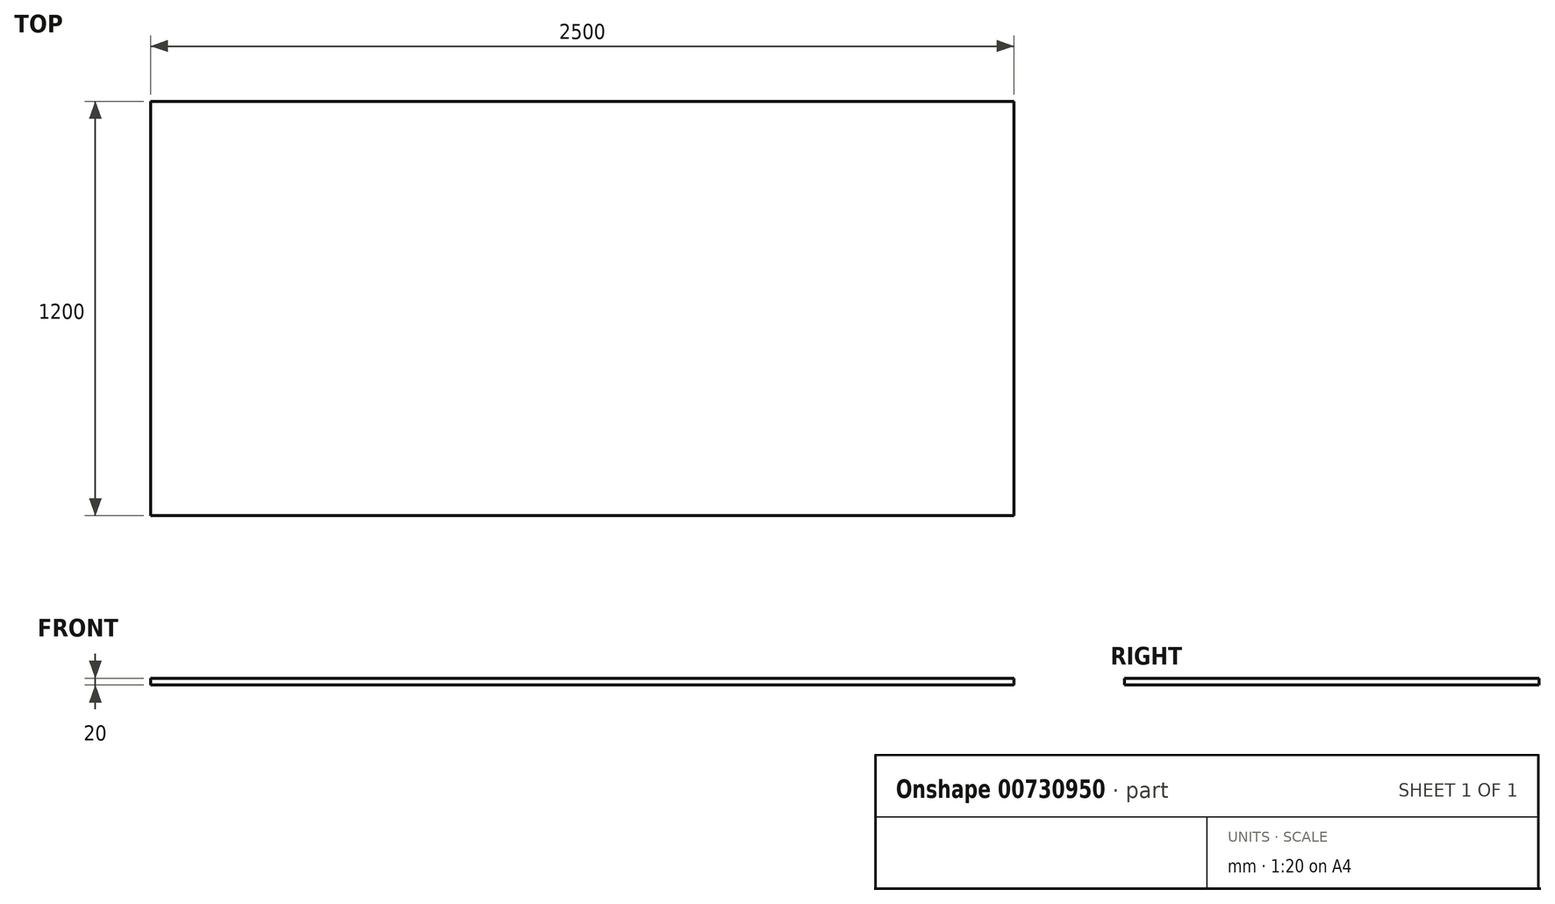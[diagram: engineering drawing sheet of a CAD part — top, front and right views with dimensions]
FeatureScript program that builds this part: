
annotation { "Feature Type Name" : "Feature", "Feature Type Description" : "" }
export const myFeature = defineFeature(function(context is Context, id is Id, definition is map)
    precondition{}
    {
        {
            var Q0;
            Q0=qCreatedBy(makeId("Front.planeOp"),FACE);
            var sketch = newSketch(context, id + "F0", { "sketchPlane" : qUnion([Q0])});
            skLineSegment(sketch, "E0.bottom", {"start": v(-1250, 0) * mm, "end": v(1250, 0) * mm});
            skLineSegment(sketch, "E0.top", {"start": v(-1250, -20) * mm, "end": v(1250, -20) * mm});
            skLineSegment(sketch, "E0.left", {"start": v(-1250, 0) * mm, "end": v(-1250, -20) * mm});
            skLineSegment(sketch, "E0.right", {"start": v(1250, 0) * mm, "end": v(1250, -20) * mm});
            skPoint(sketch, "E1", {"position": v(0, 0) * mm});
            skSolve(sketch);
        }
        {
            var Q0;
            Q0 = qSketchRegion(id + "F0", true);
            extrude(context, id + "F1", {"entities" : qUnion([Q0]), "endBound" : BoundingType.SYMMETRIC, "depth" : 1200 * mm, "offsetDistance" : 25 * mm});
        }
    });
